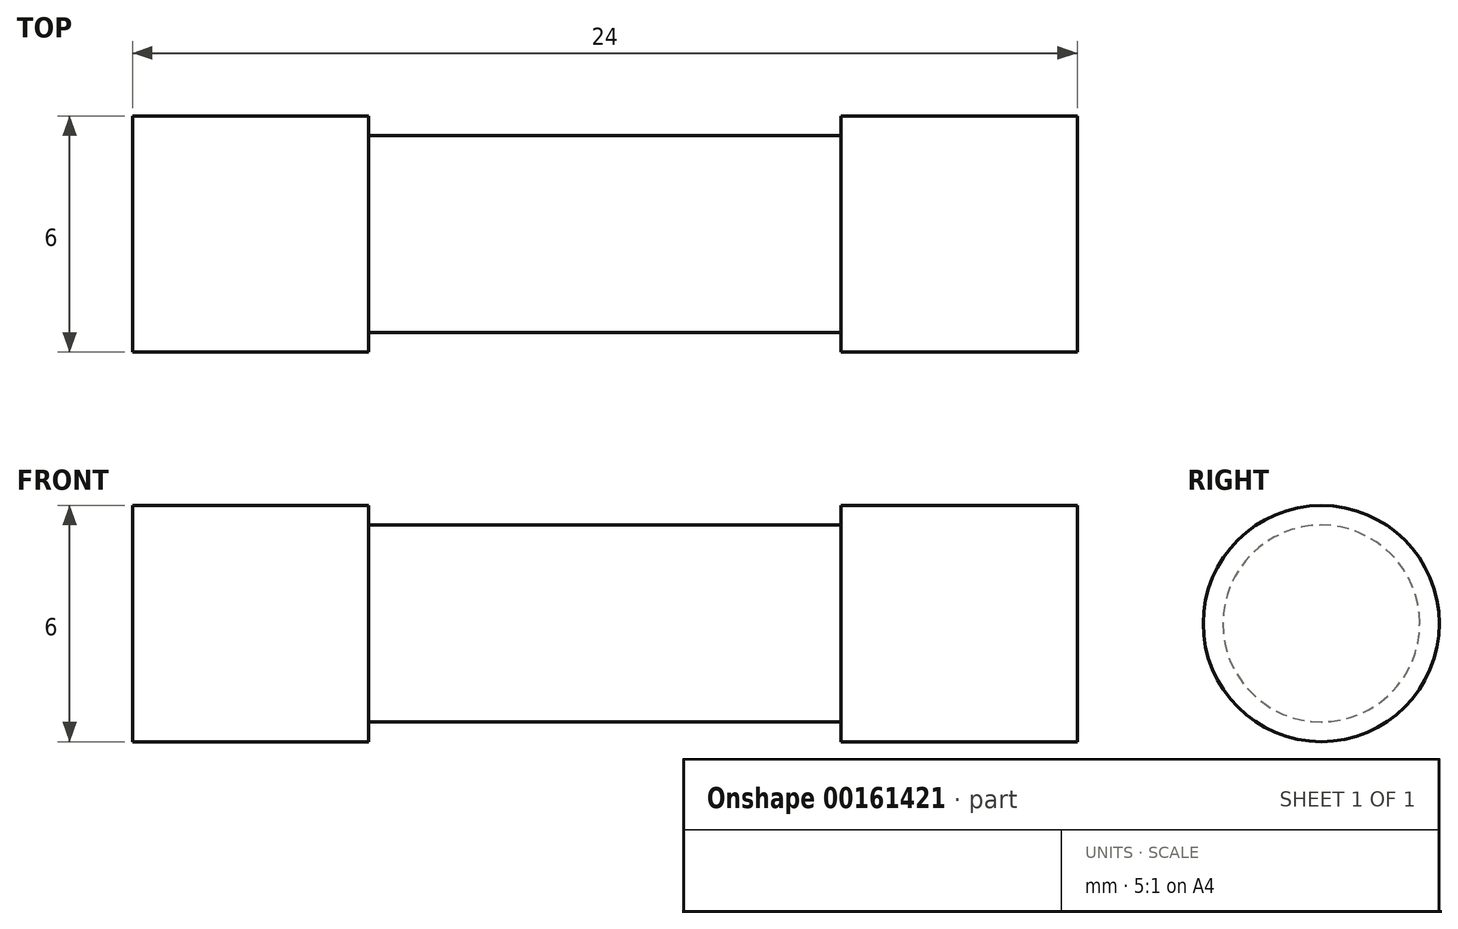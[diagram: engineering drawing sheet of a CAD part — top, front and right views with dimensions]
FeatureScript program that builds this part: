
annotation { "Feature Type Name" : "Feature", "Feature Type Description" : "" }
export const myFeature = defineFeature(function(context is Context, id is Id, definition is map)
    precondition{}
    {
        {
            var Q0;
            Q0=qCreatedBy(makeId("Right.planeOp"),FACE);
            var sketch = newSketch(context, id + "F0", { "sketchPlane" : qUnion([Q0])});
            skCircle(sketch, "E0", {"center": v(0, 0) * mm, "radius": 3 * mm});
            skSolve(sketch);
        }
        {
            var Q0;
            Q0=qSketchRegion(id+"F0",true);
            extrude(context, id + "F1", {"entities" : qUnion([Q0]), "depth" : 6 * mm});
        }
        {
            var Q0;
            Q0=makeQuery(id+"F1.opExtrude","CAP_FACE",FACE,{"disambiguationData":[OSD([sQuery(id+"F0.wireOp",EDGE,"E0")])],"isStart":false});
            var sketch = newSketch(context, id + "F2", { "sketchPlane" : qUnion([Q0])});
            skCircle(sketch, "E1", {"center": v(0, 0) * mm, "radius": 2.5 * mm});
            skSolve(sketch);
        }
        {
            var Q0;
            Q0=qSketchRegion(id+"F2",true);
            extrude(context, id + "F3", {"entities" : qUnion([Q0]), "operationType" : NewBodyOperationType.ADD, "depth" : 12 * mm});
        }
        {
            var Q0;
            Q0=makeQuery(id+"F3.opExtrude","CAP_FACE",FACE,{"disambiguationData":[OSD([sQuery(id+"F2.wireOp",EDGE,"E1")])],"isStart":false});
            var sketch = newSketch(context, id + "F4", { "sketchPlane" : qUnion([Q0])});
            skCircle(sketch, "E2", {"center": v(0, 0) * mm, "radius": 3 * mm});
            skSolve(sketch);
        }
        {
            var Q0;
            Q0=qSketchRegion(id+"F4",true);
            extrude(context, id + "F5", {"entities" : qUnion([Q0]), "operationType" : NewBodyOperationType.ADD, "depth" : 6 * mm});
        }
    });
